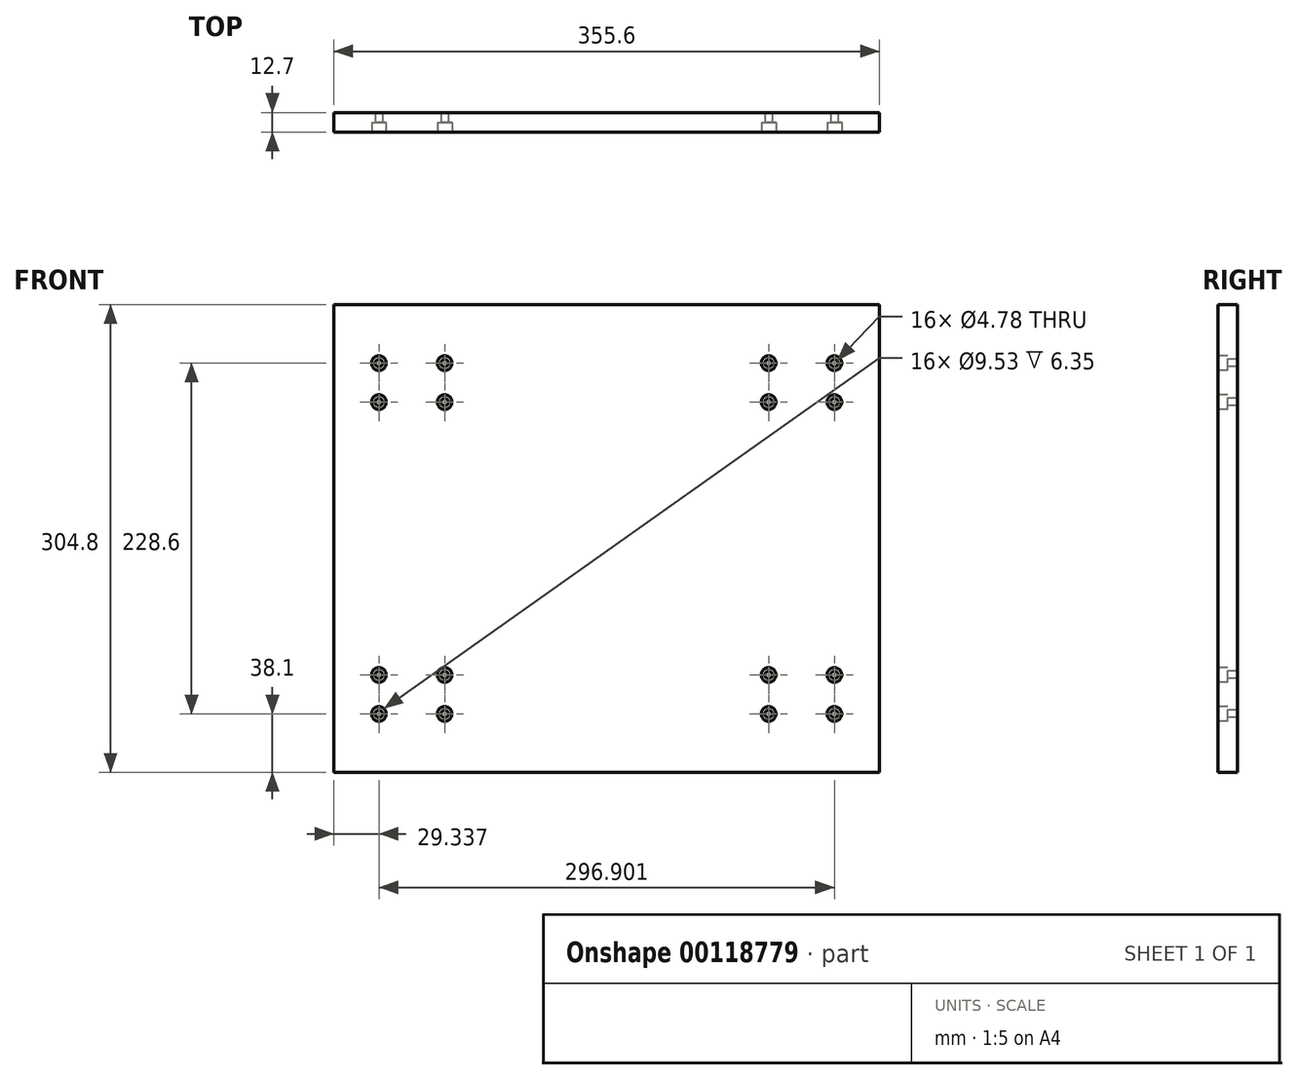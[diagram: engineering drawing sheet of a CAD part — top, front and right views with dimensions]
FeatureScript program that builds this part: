
annotation { "Feature Type Name" : "Feature", "Feature Type Description" : "" }
export const myFeature = defineFeature(function(context is Context, id is Id, definition is map)
    precondition{}
    {
        {
            var Q0;
            Q0=qCreatedBy(makeId("Front.planeOp"),FACE);
            var sketch = newSketch(context, id + "F0", { "sketchPlane" : qUnion([Q0])});
            skLineSegment(sketch, "E0.bottom", {"start": v(0, 0) * mm, "end": v(355.6, 0) * mm});
            skLineSegment(sketch, "E0.top", {"start": v(0, 304.8) * mm, "end": v(355.6, 304.8) * mm});
            skLineSegment(sketch, "E0.left", {"start": v(0, 0) * mm, "end": v(0, 304.8) * mm});
            skLineSegment(sketch, "E0.right", {"start": v(355.6, 0) * mm, "end": v(355.6, 304.8) * mm});
            skSolve(sketch);
        }
        {
            var Q0;
            Q0 = qSketchRegion(id + "F0", true);
            extrude(context, id + "F1", {"entities" : qUnion([Q0]), "depth" : 12.7 * mm});
        }
        {
            var Q0;
            Q0=makeQuery(id+"F1.opExtrude","CAP_FACE",FACE,{"disambiguationData":[OSD([sQuery(id+"F0.wireOp",EDGE,"E0.bottom"),sQuery(id+"F0.wireOp",EDGE,"E0.top"),sQuery(id+"F0.wireOp",EDGE,"E0.left"),sQuery(id+"F0.wireOp",EDGE,"E0.right")])],"isStart":false});
            var sketch = newSketch(context, id + "F2", { "sketchPlane" : qUnion([Q0])});
            skPoint(sketch, "E1", {"position": v(29.34, 266.7) * mm});
            skPoint(sketch, "E2", {"position": v(29.34, 241.3) * mm});
            skPoint(sketch, "E3", {"position": v(72.21, 266.7) * mm});
            skPoint(sketch, "E4", {"position": v(72.21, 241.3) * mm});
            skPoint(sketch, "E5", {"position": v(29.34, 63.5) * mm});
            skPoint(sketch, "E6", {"position": v(29.34, 38.1) * mm});
            skPoint(sketch, "E7", {"position": v(72.21, 63.5) * mm});
            skPoint(sketch, "E8", {"position": v(72.21, 38.1) * mm});
            skPoint(sketch, "E9", {"position": v(283.36, 266.7) * mm});
            skPoint(sketch, "E10", {"position": v(283.36, 241.3) * mm});
            skPoint(sketch, "E11", {"position": v(326.24, 266.7) * mm});
            skPoint(sketch, "E12", {"position": v(326.24, 241.3) * mm});
            skPoint(sketch, "E13", {"position": v(283.36, 63.5) * mm});
            skPoint(sketch, "E14", {"position": v(283.36, 38.1) * mm});
            skPoint(sketch, "E15", {"position": v(326.24, 63.5) * mm});
            skPoint(sketch, "E16", {"position": v(326.24, 38.1) * mm});
            skSolve(sketch);
        }
        {
            var Q0;
            Q0=sQuery(id+"F2.wireOp",VERTEX,"E3");
            var Q1;
            Q1=sQuery(id+"F2.wireOp",VERTEX,"E4");
            var Q2;
            Q2=sQuery(id+"F2.wireOp",VERTEX,"E2");
            var Q3;
            Q3=sQuery(id+"F2.wireOp",VERTEX,"E9");
            var Q4;
            Q4=sQuery(id+"F2.wireOp",VERTEX,"E10");
            var Q5;
            Q5=sQuery(id+"F2.wireOp",VERTEX,"E12");
            var Q6;
            Q6=sQuery(id+"F2.wireOp",VERTEX,"E11");
            var Q7;
            Q7=sQuery(id+"F2.wireOp",VERTEX,"E13");
            var Q8;
            Q8=sQuery(id+"F2.wireOp",VERTEX,"E16");
            var Q9;
            Q9=sQuery(id+"F2.wireOp",VERTEX,"E15");
            var Q10;
            Q10=sQuery(id+"F2.wireOp",VERTEX,"E14");
            var Q11;
            Q11=sQuery(id+"F2.wireOp",VERTEX,"E7");
            var Q12;
            Q12=sQuery(id+"F2.wireOp",VERTEX,"E8");
            var Q13;
            Q13=sQuery(id+"F2.wireOp",VERTEX,"E6");
            var Q14;
            Q14=sQuery(id+"F2.wireOp",VERTEX,"E5");
            var Q15;
            Q15=sQuery(id+"F2.wireOp",VERTEX,"E1");
            var Q16;
            Q16=makeQuery(id+"F1.opExtrude","SWEPT_BODY",BODY,{"disambiguationData":[OSD([sQuery(id+"F0.wireOp",EDGE,"E0.bottom"),sQuery(id+"F0.wireOp",EDGE,"E0.top"),sQuery(id+"F0.wireOp",EDGE,"E0.left"),sQuery(id+"F0.wireOp",EDGE,"E0.right")])]});
            hole(context, id + "F3", {"style" : HoleStyle.C_BORE, "endStyle" : HoleEndStyle.THROUGH, "holeDiameter" : 4.78 * mm, "cBoreDiameter" : 9.52 * mm, "cBoreDepth" : 6.35 * mm, "locations" : qUnion([Q0, Q1, Q2, Q3, Q4, Q5, Q6, Q7, Q8, Q9, Q10, Q11, Q12, Q13, Q14, Q15]), "scope" : qUnion([Q16]), "isTappedThrough" : true});
        }
    });
